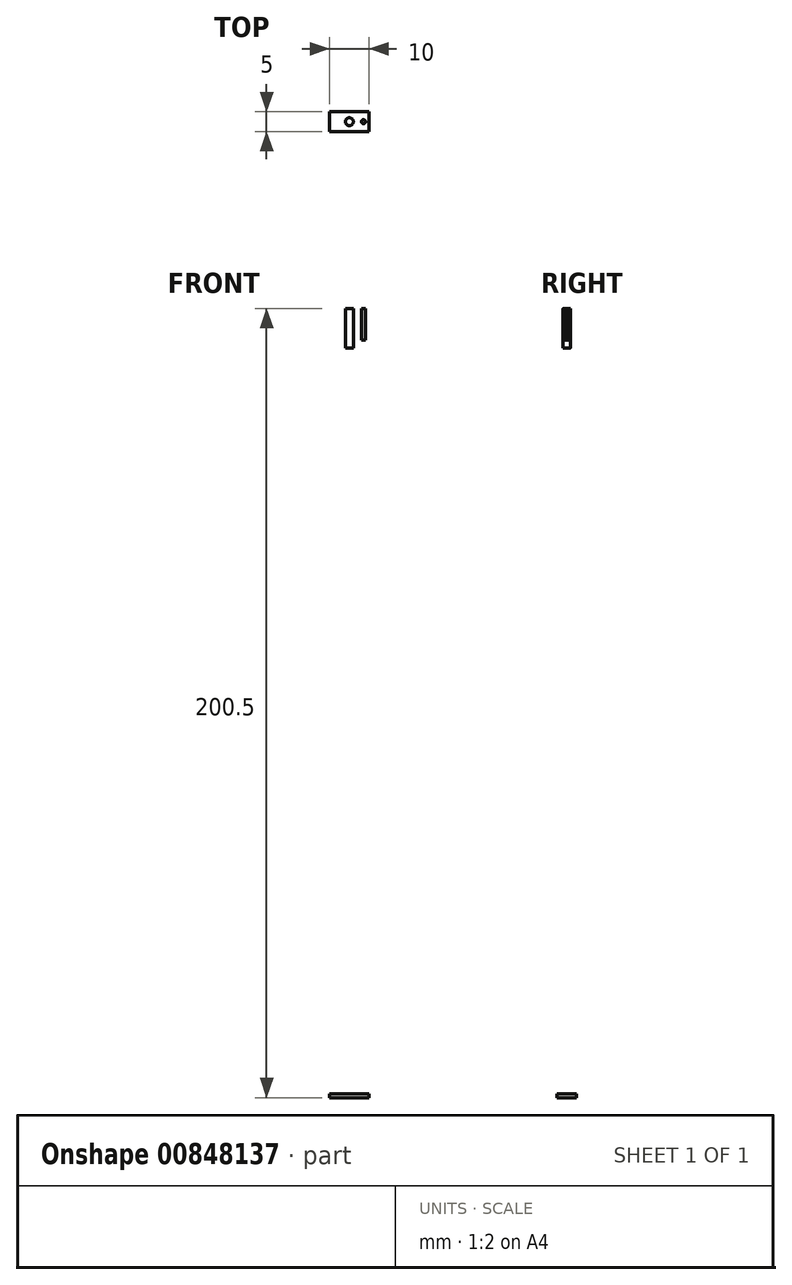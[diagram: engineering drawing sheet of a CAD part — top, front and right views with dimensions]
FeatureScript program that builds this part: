
annotation { "Feature Type Name" : "Feature", "Feature Type Description" : "" }
export const myFeature = defineFeature(function(context is Context, id is Id, definition is map)
    precondition{}
    {
        {
            var Q0;
            Q0=qCreatedBy(makeId("Top.planeOp"),FACE);
            var sketch = newSketch(context, id + "F0", { "sketchPlane" : qUnion([Q0])});
            skLineSegment(sketch, "E0.bottom", {"start": v(-5, 2.5) * mm, "end": v(5, 2.5) * mm});
            skLineSegment(sketch, "E0.top", {"start": v(-5, -2.5) * mm, "end": v(5, -2.5) * mm});
            skLineSegment(sketch, "E0.left", {"start": v(-5, 2.5) * mm, "end": v(-5, -2.5) * mm});
            skLineSegment(sketch, "E0.right", {"start": v(5, 2.5) * mm, "end": v(5, -2.5) * mm});
            skSolve(sketch);
        }
        {
            var Q0;
            Q0=makeQuery(id+"F0.imprint","IMPRINT",FACE,{"disambiguationData":[TD([[makeQuery(id+"F0.imprint","IMPRINT",EDGE,{"derivedFrom":sQuery(id+"F0.wireOp",EDGE,"E0.bottom")}),-1.0]])]});
            extrude(context, id + "F1", {"entities" : qUnion([Q0]), "endBound" : BoundingType.SYMMETRIC, "depth" : 1 * mm, "offsetDistance" : 25 * mm});
        }
        {
            var Q0;
            Q0=makeQuery(id+"F1.opExtrude","CAP_FACE",FACE,{"disambiguationData":[OSD([sQuery(id+"F0.wireOp",EDGE,"E0.bottom"),sQuery(id+"F0.wireOp",EDGE,"E0.top"),sQuery(id+"F0.wireOp",EDGE,"E0.left"),sQuery(id+"F0.wireOp",EDGE,"E0.right")])],"isStart":false});
            cPlane(context, id + "F2", {"entities" : qUnion([Q0]), "cplaneType" : CPlaneType.OFFSET, "offset" : 199.5 * mm, "width" : 150 * mm, "height" : 150 * mm});
        }
        {
            var Q0;
            Q0=qCreatedBy(id+"F2.planeOp",FACE);
            var sketch = newSketch(context, id + "F3", { "sketchPlane" : qUnion([Q0])});
            skCircle(sketch, "E1", {"center": v(0, 0) * mm, "radius": 1 * mm});
            skCircle(sketch, "E2", {"center": v(3.58, 0) * mm, "radius": 0.5 * mm});
            skSolve(sketch);
        }
        {
            var Q0;
            Q0=makeQuery(id+"F3.imprint","IMPRINT",FACE,{"disambiguationData":[TD([[makeQuery(id+"F3.imprint","IMPRINT",EDGE,{"derivedFrom":sQuery(id+"F3.wireOp",EDGE,"E1")}),1.0]])]});
            extrude(context, id + "F4", {"entities" : qUnion([Q0]), "oppositeDirection" : true, "depth" : 10 * mm, "offsetDistance" : 25 * mm});
        }
        {
            var Q0;
            Q0=makeQuery(id+"F3.imprint","IMPRINT",FACE,{"disambiguationData":[TD([[makeQuery(id+"F3.imprint","IMPRINT",EDGE,{"derivedFrom":sQuery(id+"F3.wireOp",EDGE,"E2")}),1.0]])]});
            extrude(context, id + "F5", {"entities" : qUnion([Q0]), "oppositeDirection" : true, "depth" : 8 * mm, "offsetDistance" : 25 * mm});
        }
    });
